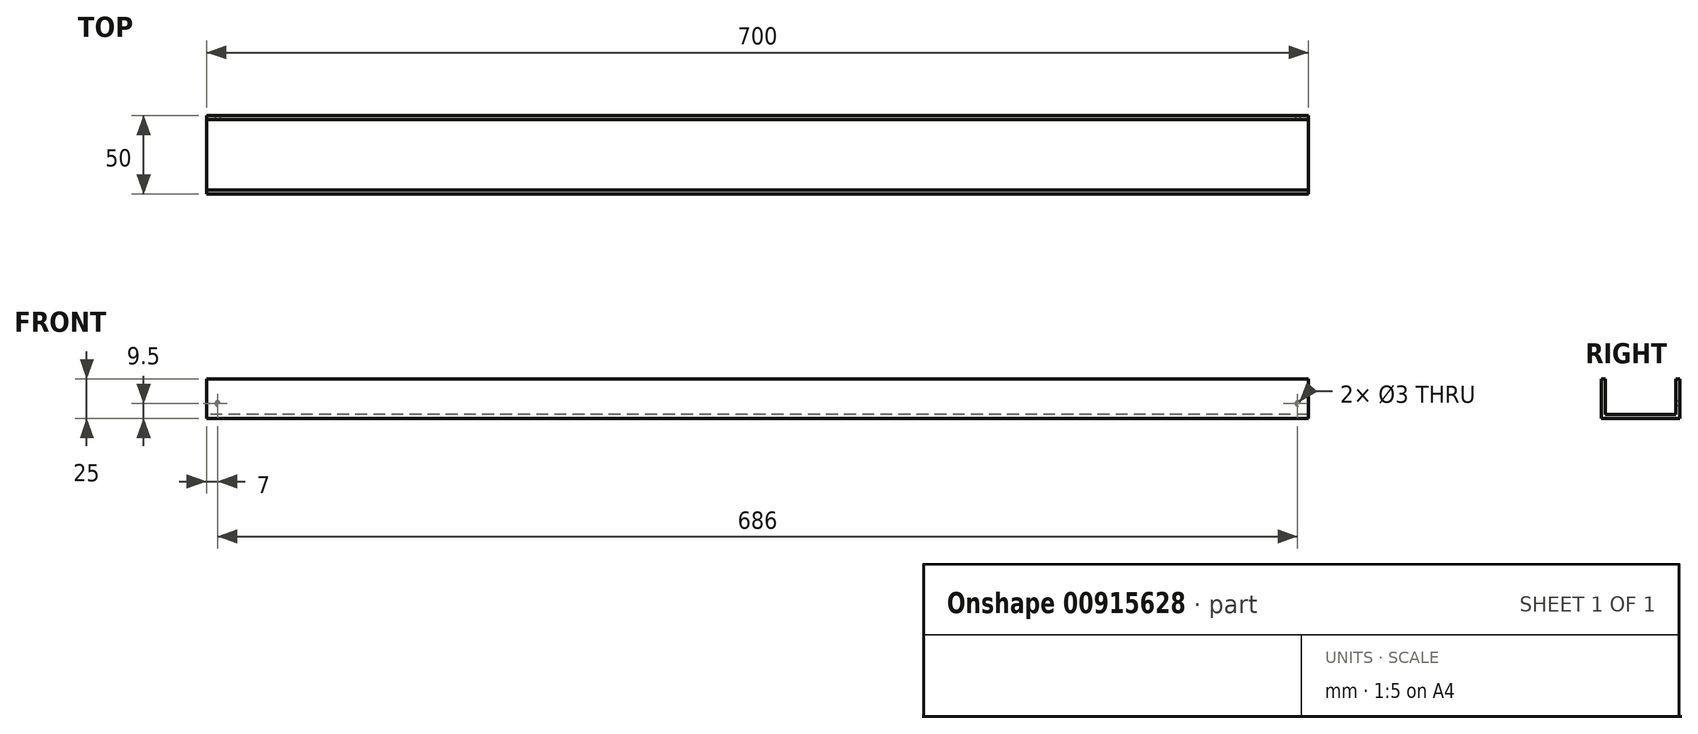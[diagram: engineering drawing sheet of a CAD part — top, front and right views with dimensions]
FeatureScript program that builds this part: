
annotation { "Feature Type Name" : "Feature", "Feature Type Description" : "" }
export const myFeature = defineFeature(function(context is Context, id is Id, definition is map)
    precondition{}
    {
        {
            var Q0;
            Q0=qCreatedBy(makeId("Right.planeOp"),FACE);
            var sketch = newSketch(context, id + "F0", { "sketchPlane" : qUnion([Q0])});
            skLineSegment(sketch, "E0.bottom", {"start": v(25, 0) * mm, "end": v(-25, 0) * mm});
            skLineSegment(sketch, "E0.top", {"start": v(25, 25) * mm, "end": v(-25, 25) * mm});
            skLineSegment(sketch, "E0.left", {"start": v(25, 0) * mm, "end": v(25, 25) * mm});
            skLineSegment(sketch, "E0.right", {"start": v(-25, 0) * mm, "end": v(-25, 25) * mm});
            skPoint(sketch, "E0.middle", {"position": v(0, 12.5) * mm});
            skLineSegment(sketch, "E1.bottom", {"start": v(22.5, 25) * mm, "end": v(-22.5, 25) * mm});
            skLineSegment(sketch, "E1.top", {"start": v(22.5, 2.5) * mm, "end": v(-22.5, 2.5) * mm});
            skLineSegment(sketch, "E1.left", {"start": v(22.5, 25) * mm, "end": v(22.5, 2.5) * mm});
            skLineSegment(sketch, "E1.right", {"start": v(-22.5, 25) * mm, "end": v(-22.5, 2.5) * mm});
            skPoint(sketch, "E1.middle", {"position": v(0, 13.75) * mm});
            skSolve(sketch);
        }
        {
            var Q0;
            Q0=makeQuery(id+"F0.imprint","IMPRINT",FACE,{"disambiguationData":[TD([[makeQuery(id+"F0.imprint","IMPRINT",EDGE,{"derivedFrom":sQuery(id+"F0.wireOp",EDGE,"E0.bottom")}),-1.0]])]});
            extrude(context, id + "F1", {"entities" : qUnion([Q0]), "depth" : 350 * mm, "offsetDistance" : 25 * mm, "hasSecondDirection" : true, "secondDirectionOppositeDirection" : true, "secondDirectionDepth" : 350 * mm});
        }
        {
            var Q0;
            Q0=makeQuery(id+"F1.opExtrude","SWEPT_FACE",FACE,{"disambiguationData":[OSD([sQuery(id+"F0.wireOp",EDGE,"E1.left")])]});
            var sketch = newSketch(context, id + "F2", { "sketchPlane" : qUnion([Q0])});
            skLineSegment(sketch, "E2.bottom", {"start": v(350, 2.5) * mm, "end": v(343, 2.5) * mm});
            skLineSegment(sketch, "E2.top", {"start": v(350, 9.5) * mm, "end": v(343, 9.5) * mm});
            skLineSegment(sketch, "E2.left", {"start": v(350, 2.5) * mm, "end": v(350, 9.5) * mm});
            skLineSegment(sketch, "E2.right", {"start": v(343, 2.5) * mm, "end": v(343, 9.5) * mm});
            skLineSegment(sketch, "E3.bottom", {"start": v(-350, 2.5) * mm, "end": v(-343, 2.5) * mm});
            skLineSegment(sketch, "E3.top", {"start": v(-350, 9.5) * mm, "end": v(-343, 9.5) * mm});
            skLineSegment(sketch, "E3.left", {"start": v(-350, 2.5) * mm, "end": v(-350, 9.5) * mm});
            skLineSegment(sketch, "E3.right", {"start": v(-343, 2.5) * mm, "end": v(-343, 9.5) * mm});
            skSolve(sketch);
        }
        {
            var Q0;
            Q0=sQuery(id+"F2.wireOp",VERTEX,"E3.top.end");
            var Q1;
            Q1=sQuery(id+"F2.wireOp",VERTEX,"E2.top.end");
            var Q2;
            Q2=makeQuery(id+"F1.opExtrude","SWEPT_BODY",BODY,{"disambiguationData":[OSD([sQuery(id+"F0.wireOp",EDGE,"E0.bottom"),sQuery(id+"F0.wireOp",EDGE,"E0.top"),sQuery(id+"F0.wireOp",EDGE,"E0.left"),sQuery(id+"F0.wireOp",EDGE,"E0.right"),sQuery(id+"F0.wireOp",EDGE,"E1.top"),sQuery(id+"F0.wireOp",EDGE,"E1.left"),sQuery(id+"F0.wireOp",EDGE,"E1.right")])]});
            hole(context, id + "F3", {"style" : HoleStyle.SIMPLE, "endStyle" : HoleEndStyle.BLIND, "holeDiameter" : 3 * mm, "majorDiameter" : 5 * mm, "holeDepth" : 10 * mm, "isTappedThrough" : true, "tappedDepth" : 12 * mm, "tapClearance" : 3, "locations" : qUnion([Q0, Q1]), "scope" : qUnion([Q2])});
        }
    });
